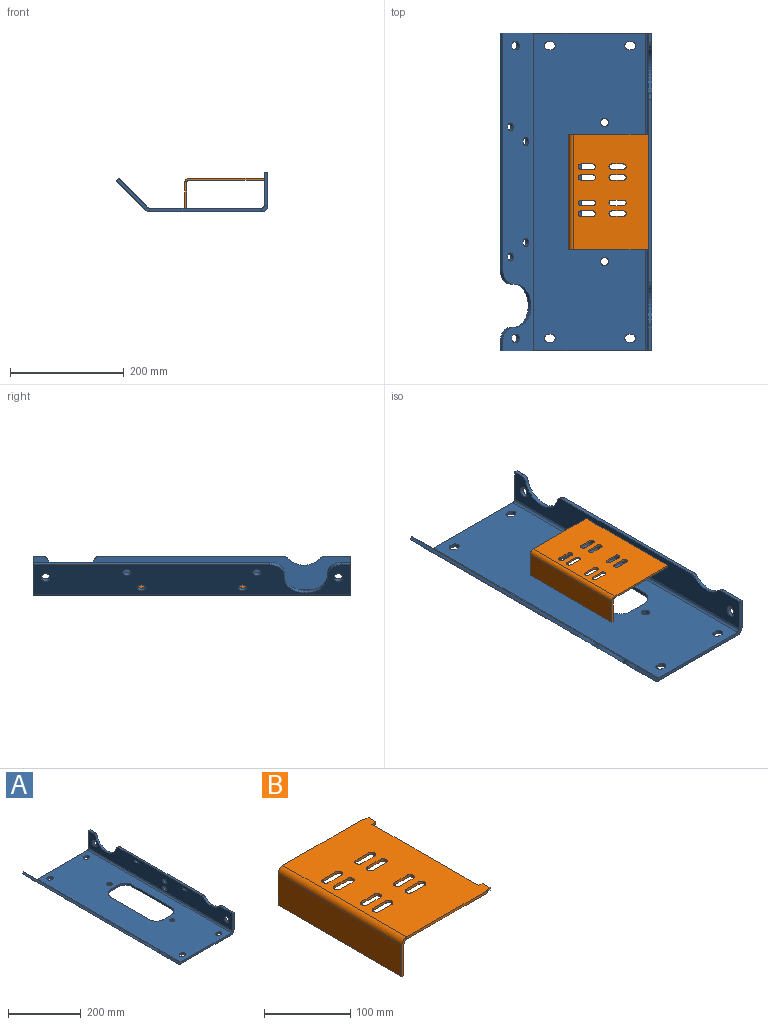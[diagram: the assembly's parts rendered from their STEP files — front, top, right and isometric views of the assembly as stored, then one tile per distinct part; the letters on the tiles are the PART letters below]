
ASSEMBLY  parts=2 mates=1
PART A: 92 faces, bbox 266.7x558.8x69.9 mm
  f0: plane 15.88x4.49mm, normal (-0.71,0,0.71), area 100.8mm2, adj f1,f20,f21,f22
  f1: plane 55.76x55.76mm, normal (0,-1,0), area 460.4mm2, adj f0,f21,f22,f88
  f2: plane 55.76x55.76mm, normal (0,1,0), area 460.4mm2, adj f3,f21,f22,f89
  f3: plane 415.93x4.49mm, normal (-0.71,0,0.71), area 2641.1mm2, adj f2,f4,f21,f22
  f4: cylinder r=25.4mm len=25.4mm, axis (0.71,0,0.71), area 253.4mm2, adj f3,f5,f21,f22
  f5: plane 8.98x8.98mm, normal (0,-1,0), area 40.3mm2, adj f4,f6,f21,f22
  f6: cylinder r=38.1mm len=76.2mm, axis (0.71,0,0.71), area 760.1mm2, adj f5,f7,f21,f22
  f7: plane 8.98x8.98mm, normal (0,1,0), area 40.3mm2, adj f6,f20,f21,f22
  f8: plane 7.87x7.87mm, normal (0,1,0), area 30.3mm2, adj f9,f19,f21,f22
  f9: cylinder r=7.14mm len=14.27mm, axis (0.71,0,0.71), area 142.4mm2, adj f8,f10,f21,f22
  f10: plane 7.87x7.87mm, normal (0,-1,0), area 30.3mm2, adj f9,f19,f21,f22
  f11: plane 7.87x7.87mm, normal (0,-1,0), area 30.3mm2, adj f12,f18,f21,f22
  f12: cylinder r=7.14mm len=14.28mm, axis (0.71,0,0.71), area 142.4mm2, adj f11,f13,f21,f22
  f13: plane 7.87x7.87mm, normal (0,1,0), area 30.3mm2, adj f12,f18,f21,f22
  f14: cylinder r=7.14mm len=14.58mm, axis (0.71,0,0.71), area 284.8mm2, adj f21,f22
  f15: cylinder r=7.14mm len=14.58mm, axis (0.71,0,0.71), area 284.8mm2, adj f21,f22
  f16: cylinder r=7.14mm len=14.58mm, axis (0.71,0,0.71), area 284.8mm2, adj f21,f22
  f17: cylinder r=7.14mm len=14.58mm, axis (0.71,0,0.71), area 284.8mm2, adj f21,f22
  f18: cylinder r=7.14mm len=14.28mm, axis (0.71,0,0.71), area 142.4mm2, adj f11,f13,f21,f22
  f19: cylinder r=7.14mm len=14.27mm, axis (0.71,0,0.71), area 142.4mm2, adj f8,f10,f21,f22
  f20: cylinder r=25.4mm len=25.4mm, axis (0.71,0,0.71), area 253.4mm2, adj f0,f7,f21,f22
  f21: plane 558.8x51.27mm, normal (0.71,0,0.71), area 34442.7mm2, adj f0,f1,f2,f3,f4,f5,f6,f7
  f22: plane 558.8x51.27mm, normal (-0.71,0,-0.71), area 34442.7mm2, adj f0,f1,f2,f3,f4,f5,f6,f7
  f23: plane 31.75x6.35mm, normal (0,1,0), area 201.6mm2, adj f24,f50,f51,f52
  f24: cylinder r=25.4mm len=25.4mm, axis (0,0,1), area 253.4mm2, adj f23,f25,f51,f52
  f25: plane 152.4x6.35mm, normal (1,0,0), area 967.7mm2, adj f24,f26,f51,f52
  f26: cylinder r=25.4mm len=25.4mm, axis (0,0,1), area 253.4mm2, adj f25,f27,f51,f52
  f27: plane 31.75x6.35mm, normal (0,-1,0), area 201.6mm2, adj f26,f28,f51,f52
  f28: cylinder r=25.4mm len=25.4mm, axis (0,0,1), area 253.4mm2, adj f27,f29,f51,f52
  f29: plane 152.4x6.35mm, normal (-1,0,0), area 967.7mm2, adj f28,f50,f51,f52
  f30: plane 6.35x4.78mm, normal (0,-1,0), area 30.3mm2, adj f31,f49,f51,f52
  f31: cylinder r=7.14mm len=14.27mm, axis (0,0,1), area 142.4mm2, adj f30,f32,f51,f52
  f32: plane 6.35x4.78mm, normal (0,1,0), area 30.3mm2, adj f31,f49,f51,f52
  f33: plane 6.35x4.78mm, normal (0,-1,0), area 30.3mm2, adj f34,f48,f51,f52
  f34: cylinder r=7.14mm len=14.27mm, axis (0,0,1), area 142.4mm2, adj f33,f35,f51,f52
  f35: plane 6.35x4.78mm, normal (0,1,0), area 30.3mm2, adj f34,f48,f51,f52
  f36: plane 6.35x4.78mm, normal (0,1,0), area 30.3mm2, adj f37,f47,f51,f52
  f37: cylinder r=7.14mm len=14.28mm, axis (0,0,1), area 142.4mm2, adj f36,f38,f51,f52
  f38: plane 6.35x4.78mm, normal (0,-1,0), area 30.3mm2, adj f37,f47,f51,f52
  f39: plane 6.35x4.78mm, normal (0,1,0), area 30.3mm2, adj f40,f46,f51,f52
  f40: cylinder r=7.14mm len=14.28mm, axis (0,0,1), area 142.4mm2, adj f39,f41,f51,f52
  f41: plane 6.35x4.78mm, normal (0,-1,0), area 30.3mm2, adj f40,f46,f51,f52
  f42: plane 196.48x6.35mm, normal (0,1,0), area 1247.7mm2, adj f51,f52,f85,f89
  f43: plane 196.48x6.35mm, normal (0,-1,0), area 1247.7mm2, adj f51,f52,f84,f88
  f44: cylinder r=7.14mm len=14.28mm, axis (0,0,1), area 284.8mm2, adj f51,f52
  f45: cylinder r=7.14mm len=14.28mm, axis (0,0,1), area 284.8mm2, adj f51,f52
  f46: cylinder r=7.14mm len=14.28mm, axis (0,0,1), area 142.4mm2, adj f39,f41,f51,f52
  f47: cylinder r=7.14mm len=14.28mm, axis (0,0,1), area 142.4mm2, adj f36,f38,f51,f52
  f48: cylinder r=7.14mm len=14.27mm, axis (0,0,1), area 142.4mm2, adj f33,f35,f51,f52
  f49: cylinder r=7.14mm len=14.27mm, axis (0,0,1), area 142.4mm2, adj f30,f32,f51,f52
  f50: cylinder r=25.4mm len=25.4mm, axis (0,0,1), area 253.4mm2, adj f23,f29,f51,f52
  f51: plane 558.8x196.48mm, normal (0,0,1), area 92341.3mm2, adj f23,f24,f25,f26,f27,f28,f29,f30
  f52: plane 558.8x196.48mm, normal (0,0,-1), area 92341.3mm2, adj f23,f24,f25,f26,f27,f28,f29,f30
  f53: plane 6.35x4.75mm, normal (0,1,0), area 30.2mm2, adj f54,f81,f82,f83
  f54: plane 14.27x6.35mm, normal (0,0,1), area 90.6mm2, adj f53,f55,f82,f83
  f55: plane 6.35x4.75mm, normal (0,-1,0), area 30.2mm2, adj f54,f81,f82,f83
  f56: plane 14.27x6.35mm, normal (0,0,-1), area 90.6mm2, adj f57,f80,f82,f83
  f57: plane 6.35x4.75mm, normal (0,1,0), area 30.2mm2, adj f56,f58,f82,f83
  f58: plane 14.27x6.35mm, normal (0,0,1), area 90.6mm2, adj f57,f80,f82,f83
  f59: plane 6.35x4.78mm, normal (0,-1,0), area 30.3mm2, adj f60,f79,f82,f83
  f60: cylinder r=7.14mm len=14.28mm, axis (-1,0,0), area 142.4mm2, adj f59,f61,f82,f83
  f61: plane 6.35x4.78mm, normal (0,1,0), area 30.3mm2, adj f60,f79,f82,f83
  f62: plane 6.35x4.78mm, normal (0,-1,0), area 30.3mm2, adj f63,f78,f82,f83
  f63: cylinder r=7.14mm len=14.27mm, axis (-1,0,0), area 142.4mm2, adj f62,f64,f82,f83
  f64: plane 6.35x4.78mm, normal (0,1,0), area 30.3mm2, adj f63,f78,f82,f83
  f65: cylinder r=41.41mm len=79.63mm, axis (-1,0,0), area 679.8mm2, adj f66,f75,f82,f83
  f66: cylinder r=11.11mm len=10.69mm, axis (-1,0,0), area 91.2mm2, adj f65,f67,f82,f83
  f67: plane 16.17x6.35mm, normal (0,0,1), area 102.7mm2, adj f66,f68,f82,f83
  f68: plane 58.75x6.35mm, normal (0,1,0), area 373.1mm2, adj f67,f82,f83,f85
  f69: plane 58.75x6.35mm, normal (0,-1,0), area 373.1mm2, adj f70,f82,f83,f84
  f70: plane 45.66x6.35mm, normal (0,0,1), area 289.9mm2, adj f69,f71,f82,f83
  f71: cylinder r=11.11mm len=8.07mm, axis (-1,0,0), area 57.3mm2, adj f70,f72,f82,f83
  f72: cylinder r=39.69mm len=57.64mm, axis (-1,0,0), area 409.6mm2, adj f71,f73,f82,f83
  f73: cylinder r=11.11mm len=8.07mm, axis (-1,0,0), area 57.3mm2, adj f72,f74,f82,f83
  f74: plane 322.18x6.35mm, normal (0,0,1), area 2045.9mm2, adj f73,f75,f82,f83
  f75: cylinder r=11.11mm len=10.69mm, axis (-1,0,0), area 91.2mm2, adj f65,f74,f82,f83
  f76: cylinder r=7.14mm len=14.28mm, axis (-1,0,0), area 284.8mm2, adj f82,f83
  f77: cylinder r=7.14mm len=14.28mm, axis (-1,0,0), area 284.8mm2, adj f82,f83
  f78: cylinder r=7.14mm len=14.27mm, axis (-1,0,0), area 142.4mm2, adj f62,f64,f82,f83
  f79: cylinder r=7.14mm len=14.28mm, axis (-1,0,0), area 142.4mm2, adj f59,f61,f82,f83
  f80: plane 6.35x4.75mm, normal (0,-1,0), area 30.2mm2, adj f56,f58,f82,f83
  f81: plane 14.27x6.35mm, normal (0,0,-1), area 90.6mm2, adj f53,f55,f82,f83
  f82: plane 558.8x58.75mm, normal (-1,0,0), area 28755.5mm2, adj f53,f54,f55,f56,f57,f58,f59,f60
  f83: plane 558.8x58.75mm, normal (1,0,0), area 28755.5mm2, adj f53,f54,f55,f56,f57,f58,f59,f60
  f84: plane 11.1x11.1mm, normal (0,-1,0), area 79mm2, adj f43,f69,f86,f87
  f85: plane 11.1x11.1mm, normal (0,1,0), area 79mm2, adj f42,f68,f86,f87
  f86: cylinder r=11.1mm len=558.8mm, axis (0,-1,0), area 9743mm2, adj f52,f83,f84,f85
  f87: cylinder r=4.75mm len=558.8mm, axis (0,-1,0), area 4169.2mm2, adj f51,f82,f84,f85
  f88: plane 7.85x7.74mm, normal (0,-1,0), area 39.5mm2, adj f1,f43,f90,f91
  f89: plane 7.85x7.74mm, normal (0,1,0), area 39.5mm2, adj f2,f42,f90,f91
  f90: cylinder r=11.1mm len=558.8mm, axis (0,-1,0), area 4871.5mm2, adj f22,f52,f88,f89
  f91: cylinder r=4.75mm len=558.8mm, axis (0,-1,0), area 2084.6mm2, adj f21,f51,f88,f89
PART B: 54 faces, bbox 146.1x203.2x52.4 mm
  f0: plane 44.45x3.43mm, normal (0,1,0), area 152.4mm2, adj f2,f3,f4,f50
  f1: plane 44.45x3.43mm, normal (0,-1,0), area 152.4mm2, adj f2,f3,f4,f51
  f2: plane 203.2x3.43mm, normal (0,0,-1), area 696.8mm2, adj f0,f1,f3,f4
  f3: plane 203.2x44.45mm, normal (1,0,0), area 9032.2mm2, adj f0,f1,f2,f52
  f4: plane 203.2x44.45mm, normal (-1,0,0), area 9032.2mm2, adj f0,f1,f2,f53
  f5: plane 12.7x3.43mm, normal (1,0,0), area 43.5mm2, adj f6,f47,f48,f49
  f6: plane 6.35x3.43mm, normal (0,-1,0), area 21.8mm2, adj f5,f7,f48,f49
  f7: plane 174.63x3.43mm, normal (1,0,0), area 598.8mm2, adj f6,f8,f48,f49
  f8: plane 6.35x3.43mm, normal (0,1,0), area 21.8mm2, adj f7,f9,f48,f49
  f9: plane 12.7x3.43mm, normal (1,0,0), area 43.5mm2, adj f8,f10,f48,f49
  f10: plane 6.35x3.43mm, normal (0,-1,0), area 21.8mm2, adj f9,f11,f48,f49
  f11: plane 3.43x1.59mm, normal (1,0,0), area 5.4mm2, adj f10,f12,f48,f49
  f12: plane 131.76x3.43mm, normal (0,-1,0), area 451.8mm2, adj f11,f48,f49,f51
  f13: plane 131.76x3.43mm, normal (0,1,0), area 451.8mm2, adj f14,f48,f49,f50
  f14: plane 3.43x1.59mm, normal (1,0,0), area 5.4mm2, adj f13,f47,f48,f49
  f15: plane 20.62x3.43mm, normal (0,-1,0), area 70.7mm2, adj f16,f46,f48,f49
  f16: cylinder r=4.76mm len=9.53mm, axis (0,0,-1), area 51.3mm2, adj f15,f17,f48,f49
  f17: plane 20.62x3.43mm, normal (0,1,0), area 70.7mm2, adj f16,f46,f48,f49
  f18: plane 20.62x3.43mm, normal (0,1,0), area 70.7mm2, adj f19,f45,f48,f49
  f19: cylinder r=4.76mm len=9.53mm, axis (0,0,-1), area 51.3mm2, adj f18,f20,f48,f49
  f20: plane 20.62x3.43mm, normal (0,-1,0), area 70.7mm2, adj f19,f45,f48,f49
  f21: plane 20.62x3.43mm, normal (0,1,0), area 70.7mm2, adj f22,f44,f48,f49
  f22: cylinder r=4.76mm len=9.53mm, axis (0,0,-1), area 51.3mm2, adj f21,f23,f48,f49
  f23: plane 20.62x3.43mm, normal (0,-1,0), area 70.7mm2, adj f22,f44,f48,f49
  f24: plane 20.62x3.43mm, normal (0,-1,0), area 70.7mm2, adj f25,f43,f48,f49
  f25: cylinder r=4.76mm len=9.53mm, axis (0,0,-1), area 51.3mm2, adj f24,f26,f48,f49
  f26: plane 20.62x3.43mm, normal (0,1,0), area 70.7mm2, adj f25,f43,f48,f49
  f27: plane 20.63x3.43mm, normal (0,-1,0), area 70.7mm2, adj f28,f42,f48,f49
  f28: cylinder r=4.76mm len=9.53mm, axis (0,0,-1), area 51.3mm2, adj f27,f29,f48,f49
  f29: plane 20.63x3.43mm, normal (0,1,0), area 70.7mm2, adj f28,f42,f48,f49
  f30: plane 20.63x3.43mm, normal (0,1,0), area 70.7mm2, adj f31,f41,f48,f49
  f31: cylinder r=4.76mm len=9.53mm, axis (0,0,-1), area 51.3mm2, adj f30,f32,f48,f49
  f32: plane 20.63x3.43mm, normal (0,-1,0), area 70.7mm2, adj f31,f41,f48,f49
  f33: plane 20.63x3.43mm, normal (0,-1,0), area 70.7mm2, adj f34,f40,f48,f49
  f34: cylinder r=4.76mm len=9.53mm, axis (0,0,-1), area 51.3mm2, adj f33,f35,f48,f49
  f35: plane 20.63x3.43mm, normal (0,1,0), area 70.7mm2, adj f34,f40,f48,f49
  f36: plane 20.63x3.43mm, normal (0,-1,0), area 70.7mm2, adj f37,f39,f48,f49
  f37: cylinder r=4.76mm len=9.53mm, axis (0,0,-1), area 51.3mm2, adj f36,f38,f48,f49
  f38: plane 20.63x3.43mm, normal (0,1,0), area 70.7mm2, adj f37,f39,f48,f49
  f39: cylinder r=4.76mm len=9.53mm, axis (0,0,-1), area 51.3mm2, adj f36,f38,f48,f49
  f40: cylinder r=4.76mm len=9.53mm, axis (0,0,-1), area 51.3mm2, adj f33,f35,f48,f49
  f41: cylinder r=4.76mm len=9.53mm, axis (0,0,-1), area 51.3mm2, adj f30,f32,f48,f49
  f42: cylinder r=4.76mm len=9.53mm, axis (0,0,-1), area 51.3mm2, adj f27,f29,f48,f49
  f43: cylinder r=4.76mm len=9.53mm, axis (0,0,-1), area 51.3mm2, adj f24,f26,f48,f49
  f44: cylinder r=4.76mm len=9.53mm, axis (0,0,-1), area 51.3mm2, adj f21,f23,f48,f49
  f45: cylinder r=4.76mm len=9.53mm, axis (0,0,-1), area 51.3mm2, adj f18,f20,f48,f49
  f46: cylinder r=4.76mm len=9.53mm, axis (0,0,-1), area 51.3mm2, adj f15,f17,f48,f49
  f47: plane 6.35x3.43mm, normal (0,1,0), area 21.8mm2, adj f5,f14,f48,f49
  f48: plane 203.2x138.11mm, normal (0,0,-1), area 24793.8mm2, adj f5,f6,f7,f8,f9,f10,f11,f12
  f49: plane 203.2x138.11mm, normal (0,0,1), area 24793.8mm2, adj f5,f6,f7,f8,f9,f10,f11,f12
  f50: plane 7.94x7.94mm, normal (0,1,0), area 33.5mm2, adj f0,f13,f52,f53
  f51: plane 7.94x7.94mm, normal (0,-1,0), area 33.5mm2, adj f1,f12,f52,f53
  f52: cylinder r=4.51mm len=203.2mm, axis (0,-1,0), area 1439mm2, adj f3,f48,f50,f51
  f53: cylinder r=7.94mm len=203.2mm, axis (0,-1,0), area 2533.5mm2, adj f4,f49,f50,f51
PLACE A t=(65.43,211.69,-164.24)mm
PLACE B t=(52.49,33.89,-146.39)mm
MATE fastened B.f9 <-> A.f83  axis (1,0,0) through (124.52,-161.38,-113.45)mm
